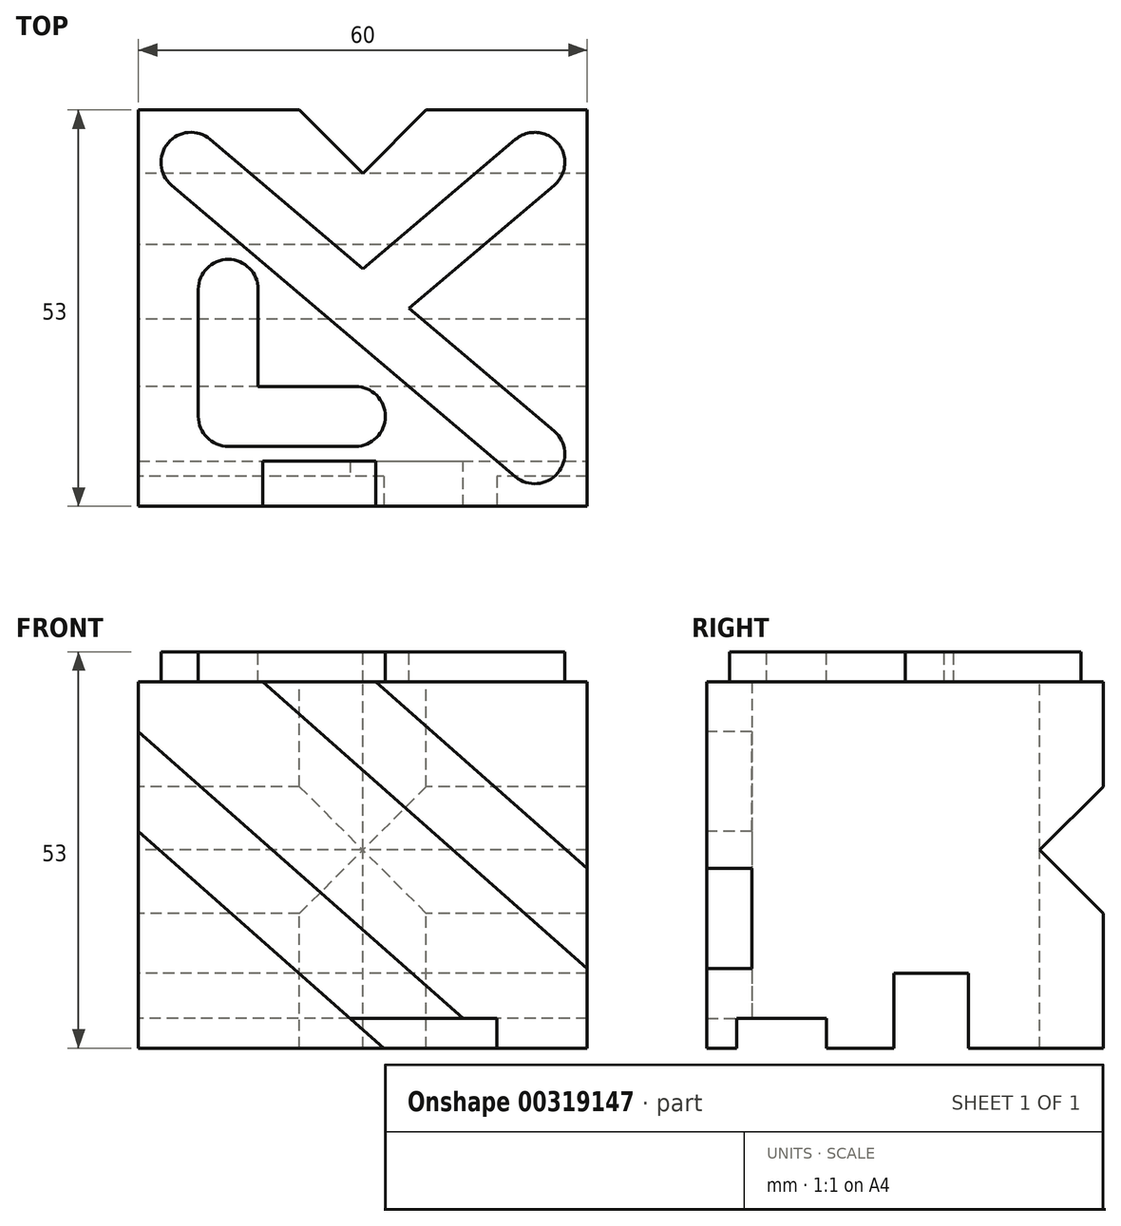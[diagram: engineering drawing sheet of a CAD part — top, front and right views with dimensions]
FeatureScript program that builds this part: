
annotation { "Feature Type Name" : "Feature", "Feature Type Description" : "" }
export const myFeature = defineFeature(function(context is Context, id is Id, definition is map)
    precondition{}
    {
        {
            var Q0;
            Q0=qCreatedBy(makeId("Right.planeOp"),FACE);
            var sketch = newSketch(context, id + "F0", { "sketchPlane" : qUnion([Q0])});
            skLineSegment(sketch, "E0.bottom", {"start": v(53, 0) * mm, "end": v(0, 0) * mm});
            skLineSegment(sketch, "E0.top", {"start": v(53, 53) * mm, "end": v(0, 53) * mm});
            skLineSegment(sketch, "E0.left", {"start": v(53, 0) * mm, "end": v(53, 53) * mm});
            skLineSegment(sketch, "E0.right", {"start": v(0, 0) * mm, "end": v(0, 53) * mm});
            skSolve(sketch);
        }
        {
            var Q0;
            Q0=makeQuery(id+"F0.imprint","IMPRINT",FACE,{"disambiguationData":[TD([[makeQuery(id+"F0.imprint","IMPRINT",EDGE,{"derivedFrom":sQuery(id+"F0.wireOp",EDGE,"E0.bottom")}),-1.0]])]});
            extrude(context, id + "F1", {"entities" : qUnion([Q0]), "depth" : 60 * mm});
        }
        {
            var Q0;
            Q0=makeQuery(id+"F1.opExtrude","SWEPT_FACE",FACE,{"disambiguationData":[OSD([sQuery(id+"F0.wireOp",EDGE,"E0.top")])]});
            var sketch = newSketch(context, id + "F2", { "sketchPlane" : qUnion([Q0])});
            skLineSegment(sketch, "E1", {"start": v(12, 29) * mm, "end": v(12, 12) * mm, "construction": true});
            skLineSegment(sketch, "E2", {"start": v(12, 12) * mm, "end": v(29, 12) * mm, "construction": true});
            skArc(sketch, "E3.0.startCap", {"start": v(8, 29) * mm, "mid": v(12, 33) * mm, "end": v(16, 29) * mm});
            skArc(sketch, "E3.0.endCap", {"start": v(16, 12) * mm, "mid": v(12, 8) * mm, "end": v(8, 12) * mm});
            skLineSegment(sketch, "E3.0.left", {"start": v(16, 29) * mm, "end": v(16, 16) * mm});
            skLineSegment(sketch, "E3.0.right", {"start": v(8, 29) * mm, "end": v(8, 12) * mm});
            skArc(sketch, "E3.1.startCap", {"start": v(12, 8) * mm, "mid": v(8, 12) * mm, "end": v(12, 16) * mm});
            skArc(sketch, "E3.1.endCap", {"start": v(29, 16) * mm, "mid": v(33, 12) * mm, "end": v(29, 8) * mm});
            skLineSegment(sketch, "E3.1.left", {"start": v(16, 16) * mm, "end": v(29, 16) * mm});
            skLineSegment(sketch, "E3.1.right", {"start": v(12, 8) * mm, "end": v(29, 8) * mm});
            skLineSegment(sketch, "E4.bottom", {"start": v(60, 0) * mm, "end": v(53, 0) * mm, "construction": true});
            skLineSegment(sketch, "E4.top", {"start": v(60, 7) * mm, "end": v(53, 7) * mm, "construction": true});
            skLineSegment(sketch, "E4.left", {"start": v(60, 0) * mm, "end": v(60, 7) * mm, "construction": true});
            skLineSegment(sketch, "E4.right", {"start": v(53, 0) * mm, "end": v(53, 7) * mm, "construction": true});
            skLineSegment(sketch, "E5.bottom", {"start": v(0, 53) * mm, "end": v(7, 53) * mm, "construction": true});
            skLineSegment(sketch, "E5.top", {"start": v(0, 46) * mm, "end": v(7, 46) * mm, "construction": true});
            skLineSegment(sketch, "E5.left", {"start": v(0, 53) * mm, "end": v(0, 46) * mm, "construction": true});
            skLineSegment(sketch, "E5.right", {"start": v(7, 53) * mm, "end": v(7, 46) * mm, "construction": true});
            skLineSegment(sketch, "E6", {"start": v(7, 46) * mm, "end": v(53, 7) * mm, "construction": true});
            skArc(sketch, "E7.0.startCap", {"start": v(4.41, 42.95) * mm, "mid": v(3.95, 48.59) * mm, "end": v(9.59, 49.05) * mm});
            skArc(sketch, "E7.0.endCap", {"start": v(55.59, 10.05) * mm, "mid": v(56.05, 4.41) * mm, "end": v(50.41, 3.95) * mm});
            skLineSegment(sketch, "E7.0.left", {"start": v(9.59, 49.05) * mm, "end": v(30, 31.74) * mm});
            skLineSegment(sketch, "E7.0.right", {"start": v(4.41, 42.95) * mm, "end": v(50.41, 3.95) * mm});
            skPoint(sketch, "E8", {"position": v(30, 26.5) * mm});
            skLineSegment(sketch, "E9", {"start": v(30, 26.5) * mm, "end": v(53, 46) * mm, "construction": true});
            skArc(sketch, "E10.0.startCap", {"start": v(32.59, 23.45) * mm, "mid": v(26.95, 23.91) * mm, "end": v(27.41, 29.55) * mm});
            skArc(sketch, "E10.0.endCap", {"start": v(50.41, 49.05) * mm, "mid": v(56.05, 48.59) * mm, "end": v(55.59, 42.95) * mm});
            skLineSegment(sketch, "E10.0.left", {"start": v(27.41, 29.55) * mm, "end": v(50.41, 49.05) * mm});
            skLineSegment(sketch, "E10.0.right", {"start": v(32.59, 23.45) * mm, "end": v(55.59, 42.95) * mm});
            skLineSegment(sketch, "E11.trimOffspring", {"start": v(33.1, 29.12) * mm, "end": v(55.59, 10.05) * mm});
            skLineSegment(sketch, "E12", {"start": v(21.52, 53) * mm, "end": v(30, 44.52) * mm});
            skPoint(sketch, "E12.endSnap0", {"position": v(30, 53) * mm});
            skLineSegment(sketch, "E13", {"start": v(30, 79.74) * mm, "end": v(30, 95.62) * mm, "construction": true});
            skLineSegment(sketch, "E14.MirrorCS", {"start": v(38.48, 53) * mm, "end": v(30, 44.52) * mm});
            skPoint(sketch, "E15", {"position": v(0, 23.4) * mm});
            skPoint(sketch, "E16", {"position": v(60, 20.14) * mm});
            skSolve(sketch);
        }
        {
            var Q0;
            {var subQ5=sQuery(id+"F2.wireOp",EDGE,"E7.0.startCap");Q0=makeQuery(id+"F2.imprint","IMPRINT",FACE,{"disambiguationData":[TD([[makeQuery(id+"F2.imprint","IMPRINT",EDGE,{"derivedFrom":subQ5}),-1.0]])]});}
            var Q1;
            {var subQ7=sQuery(id+"F2.wireOp",EDGE,"E7.0.endCap");Q1=makeQuery(id+"F2.imprint","IMPRINT",FACE,{"disambiguationData":[TD([[makeQuery(id+"F2.imprint","IMPRINT",EDGE,{"derivedFrom":subQ7}),-1.0]])]});}
            var Q2;
            {var subQ4=sQuery(id+"F2.wireOp",EDGE,"E10.0.endCap");Q2=makeQuery(id+"F2.imprint","IMPRINT",FACE,{"disambiguationData":[TD([[makeQuery(id+"F2.imprint","IMPRINT",EDGE,{"derivedFrom":subQ4}),-1.0]])]});}
            var Q3;
            Q3=makeQuery(id+"F2.imprint","IMPRINT",FACE,{"disambiguationData":[TD([[makeQuery(id+"F2.imprint","IMPRINT",EDGE,{"derivedFrom":sQuery(id+"F2.wireOp",EDGE,"E3.0.startCap")}),-1.0]])]});
            extrude(context, id + "F3", {"entities" : qUnion([Q0, Q1, Q2, Q3]), "operationType" : NewBodyOperationType.REMOVE, "oppositeDirection" : true, "depth" : 4 * mm});
        }
        {
            var Q0;
            {var subQ0=sQuery(id+"F2.wireOp",EDGE,"E12");Q0=makeQuery(id+"F2.imprint","IMPRINT",FACE,{"disambiguationData":[TD([[makeQuery(id+"F2.imprint","IMPRINT",EDGE,{"derivedFrom":subQ0}),1.0]])]});}
            var Q1;
            Q1=makeQuery(id+"F1.opExtrude","CAP_VERTEX",VERTEX,{"disambiguationData":[OSD([sQuery(id+"F0.wireOp",EDGE,"E0.bottom"),sQuery(id+"F0.wireOp",EDGE,"E0.left")])],"isStart":false});
            extrude(context, id + "F4", {"entities" : qUnion([Q0]), "operationType" : NewBodyOperationType.REMOVE, "endBound" : BoundingType.UP_TO_VERTEX, "oppositeDirection" : true, "endBoundEntityVertex" : qUnion([Q1]), "depth" : 25 * mm});
        }
        {
            var Q0;
            Q0=makeQuery(id+"F1.opExtrude","SWEPT_FACE",FACE,{"disambiguationData":[OSD([sQuery(id+"F0.wireOp",EDGE,"E0.right")])]});
            var sketch = newSketch(context, id + "F5", { "sketchPlane" : qUnion([Q0])});
            skLineSegment(sketch, "E17.bottom", {"start": v(0, 53) * mm, "end": v(60, 53) * mm});
            skLineSegment(sketch, "E17.top", {"start": v(0, 0) * mm, "end": v(60, 0) * mm});
            skLineSegment(sketch, "E17.left", {"start": v(0, 53) * mm, "end": v(0, 0) * mm});
            skLineSegment(sketch, "E17.right", {"start": v(60, 53) * mm, "end": v(60, 0) * mm});
            skLineSegment(sketch, "E18", {"start": v(0, 53) * mm, "end": v(60, 0) * mm, "construction": true});
            skLineSegment(sketch, "E19", {"start": v(0, 42.33) * mm, "end": v(47.92, 0) * mm});
            skLineSegment(sketch, "E20", {"start": v(0, 28.98) * mm, "end": v(32.81, 0) * mm});
            skLineSegment(sketch, "E21", {"start": v(27.19, 53) * mm, "end": v(60, 24.02) * mm});
            skLineSegment(sketch, "E22", {"start": v(12.08, 53) * mm, "end": v(60, 10.67) * mm});
            skSolve(sketch);
        }
        {
            var Q0;
            {var subQ0=sQuery(id+"F5.wireOp",EDGE,"E21");Q0=makeQuery(id+"F5.imprint","IMPRINT",FACE,{"disambiguationData":[TD([[makeQuery(id+"F5.imprint","IMPRINT",EDGE,{"derivedFrom":subQ0}),-1.0]])]});}
            var Q1;
            {var subQ0=sQuery(id+"F5.wireOp",EDGE,"E19");Q1=makeQuery(id+"F5.imprint","IMPRINT",FACE,{"disambiguationData":[TD([[makeQuery(id+"F5.imprint","IMPRINT",EDGE,{"derivedFrom":subQ0}),-1.0]])]});}
            extrude(context, id + "F6", {"entities" : qUnion([Q0, Q1]), "operationType" : NewBodyOperationType.REMOVE, "oppositeDirection" : true, "depth" : 6 * mm});
        }
        {
            var Q0;
            Q0=makeQuery(id+"F1.opExtrude","CAP_FACE",FACE,{"disambiguationData":[OSD([sQuery(id+"F0.wireOp",EDGE,"E0.bottom"),sQuery(id+"F0.wireOp",EDGE,"E0.top"),sQuery(id+"F0.wireOp",EDGE,"E0.left"),sQuery(id+"F0.wireOp",EDGE,"E0.right")])],"isStart":true});
            var sketch = newSketch(context, id + "F7", { "sketchPlane" : qUnion([Q0])});
            skLineSegment(sketch, "E23", {"start": v(-53, 34.98) * mm, "end": v(-44.52, 26.5) * mm});
            skPoint(sketch, "E23.endSnap0", {"position": v(-53, 26.5) * mm});
            skLineSegment(sketch, "E24", {"start": v(-76.86, 26.5) * mm, "end": v(-99.72, 26.5) * mm, "construction": true});
            skLineSegment(sketch, "E25.MirrorCS", {"start": v(-53, 18.02) * mm, "end": v(-44.52, 26.5) * mm});
            skLineSegment(sketch, "E26", {"start": v(-53, 18.02) * mm, "end": v(-53, 34.98) * mm});
            skSolve(sketch);
        }
        {
            var Q0;
            Q0=makeQuery(id+"F7.imprint","IMPRINT",FACE,{"disambiguationData":[TD([[makeQuery(id+"F7.imprint","IMPRINT",EDGE,{"derivedFrom":sQuery(id+"F7.wireOp",EDGE,"E23")}),-1.0]])]});
            var Q1;
            Q1=makeQuery(id+"F1.opExtrude","CAP_VERTEX",VERTEX,{"disambiguationData":[OSD([sQuery(id+"F0.wireOp",EDGE,"E0.bottom"),sQuery(id+"F0.wireOp",EDGE,"E0.left")])],"isStart":false});
            extrude(context, id + "F8", {"entities" : qUnion([Q0]), "operationType" : NewBodyOperationType.REMOVE, "endBound" : BoundingType.UP_TO_VERTEX, "oppositeDirection" : true, "endBoundEntityVertex" : qUnion([Q1]), "depth" : 25 * mm});
        }
        {
            var Q0;
            Q0=makeQuery(id+"F1.opExtrude","SWEPT_FACE",FACE,{"disambiguationData":[OSD([sQuery(id+"F0.wireOp",EDGE,"E0.bottom")])]});
            var sketch = newSketch(context, id + "F9", { "sketchPlane" : qUnion([Q0])});
            skLineSegment(sketch, "E27.bottom", {"start": v(60, -53) * mm, "end": v(0, -53) * mm});
            skLineSegment(sketch, "E27.top", {"start": v(60, 0) * mm, "end": v(0, 0) * mm});
            skLineSegment(sketch, "E27.left", {"start": v(60, -53) * mm, "end": v(60, 0) * mm});
            skLineSegment(sketch, "E27.right", {"start": v(0, -53) * mm, "end": v(0, 0) * mm});
            skLineSegment(sketch, "E28.top", {"start": v(60, -45) * mm, "end": v(0, -45) * mm});
            skLineSegment(sketch, "E28.left", {"start": v(60, -53) * mm, "end": v(60, -45) * mm});
            skLineSegment(sketch, "E28.right", {"start": v(0, -53) * mm, "end": v(0, -45) * mm});
            skLineSegment(sketch, "E29.top", {"start": v(60, -35) * mm, "end": v(0, -35) * mm});
            skLineSegment(sketch, "E29.left", {"start": v(60, -45) * mm, "end": v(60, -35) * mm});
            skLineSegment(sketch, "E29.right", {"start": v(0, -45) * mm, "end": v(0, -35) * mm});
            skLineSegment(sketch, "E30.top", {"start": v(60, -25) * mm, "end": v(0, -25) * mm});
            skLineSegment(sketch, "E30.left", {"start": v(60, -35) * mm, "end": v(60, -25) * mm});
            skLineSegment(sketch, "E30.right", {"start": v(0, -35) * mm, "end": v(0, -25) * mm});
            skLineSegment(sketch, "E31.top", {"start": v(60, -16) * mm, "end": v(0, -16) * mm});
            skLineSegment(sketch, "E31.left", {"start": v(60, -25) * mm, "end": v(60, -16) * mm});
            skLineSegment(sketch, "E31.right", {"start": v(0, -25) * mm, "end": v(0, -16) * mm});
            skLineSegment(sketch, "E32.top", {"start": v(60, -4) * mm, "end": v(0, -4) * mm});
            skLineSegment(sketch, "E32.left", {"start": v(60, -16) * mm, "end": v(60, -4) * mm});
            skLineSegment(sketch, "E32.right", {"start": v(0, -16) * mm, "end": v(0, -4) * mm});
            skSolve(sketch);
        }
        {
            var Q0;
            Q0=makeQuery(id+"F9.imprint","IMPRINT",FACE,{"disambiguationData":[TD([[makeQuery(id+"F9.imprint","IMPRINT",EDGE,{"derivedFrom":sQuery(id+"F9.wireOp",EDGE,"E31.top")}),-1.0]])]});
            var Q1;
            {var subQ1=sQuery(id+"F9.wireOp",EDGE,"E28.left");Q1=makeQuery(id+"F9.imprint","IMPRINT",FACE,{"disambiguationData":[TD([[makeQuery(id+"F9.imprint","IMPRINT",EDGE,{"derivedFrom":subQ1}),1.0]])]});}
            extrude(context, id + "F10", {"entities" : qUnion([Q0, Q1]), "operationType" : NewBodyOperationType.REMOVE, "oppositeDirection" : true, "depth" : 4 * mm});
        }
        {
            var Q0;
            Q0=makeQuery(id+"F9.imprint","IMPRINT",FACE,{"disambiguationData":[TD([[makeQuery(id+"F9.imprint","IMPRINT",EDGE,{"derivedFrom":sQuery(id+"F9.wireOp",EDGE,"E29.top")}),-1.0]])]});
            extrude(context, id + "F11", {"entities" : qUnion([Q0]), "operationType" : NewBodyOperationType.REMOVE, "oppositeDirection" : true, "depth" : 10 * mm});
        }
        {
            var Q0;
            Q0=makeQuery(id+"F10.boolean.opBoolean","COPY",FACE,{"derivedFrom":makeQuery(id+"F10.opExtrude","SWEPT_FACE",FACE,{"disambiguationData":[OSD([sQuery(id+"F5.wireOp",EDGE,"E17.top"),sQuery(id+"F5.wireOp",EDGE,"E19")])]})});
            extrude(context, id + "F12", {"entities" : qUnion([Q0]), "operationType" : NewBodyOperationType.REMOVE, "oppositeDirection" : true, "depth" : 25 * mm});
        }
    });
